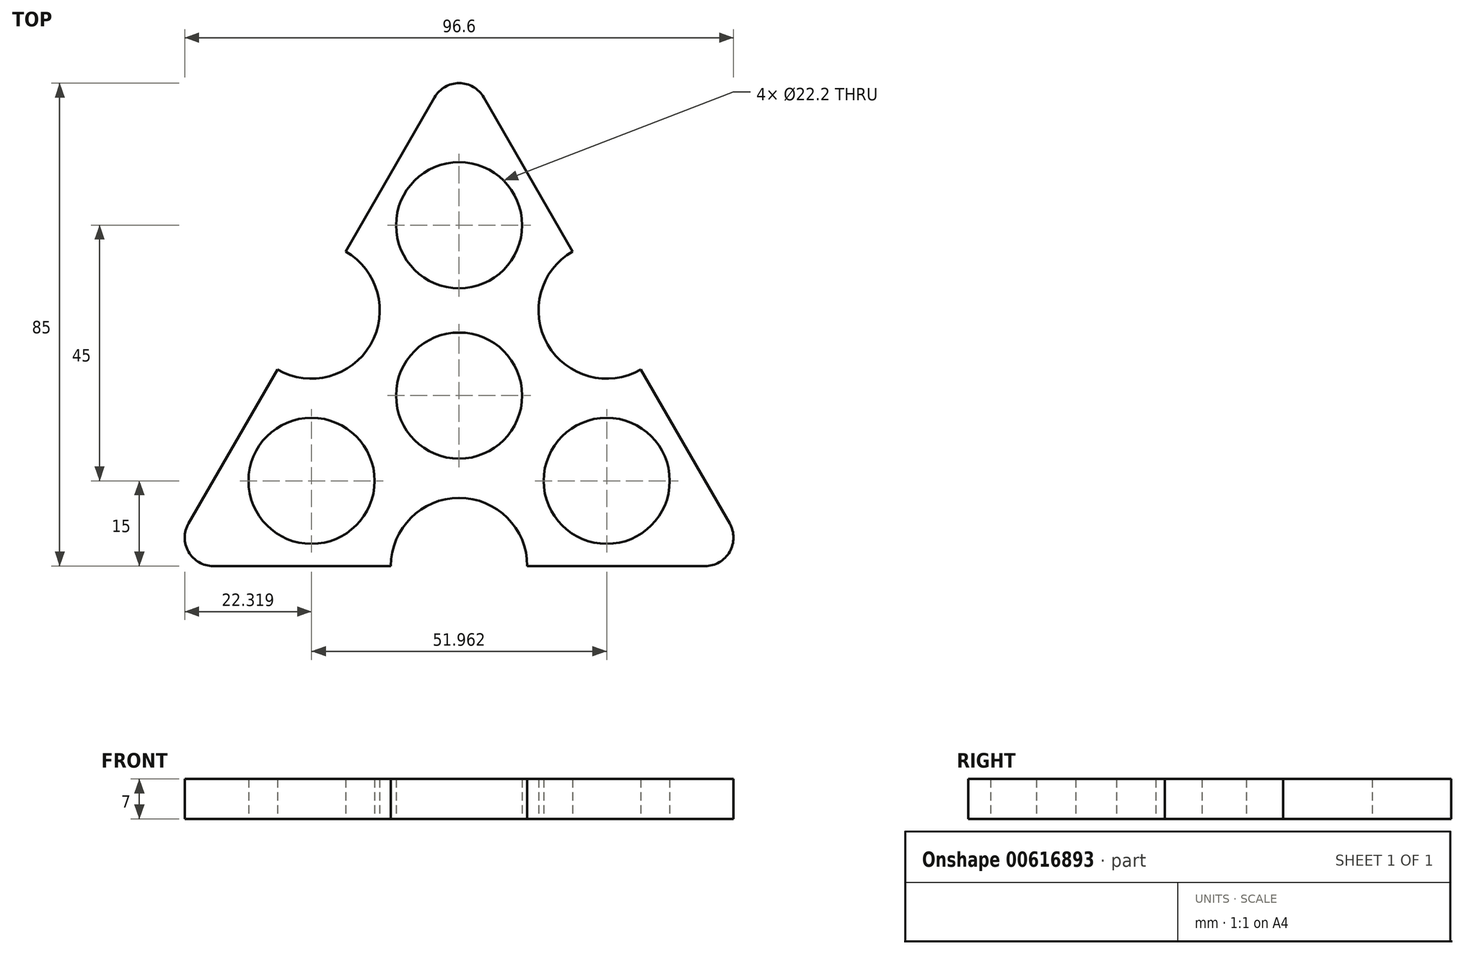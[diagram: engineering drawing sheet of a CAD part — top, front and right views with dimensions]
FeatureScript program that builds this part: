
annotation { "Feature Type Name" : "Feature", "Feature Type Description" : "" }
export const myFeature = defineFeature(function(context is Context, id is Id, definition is map)
    precondition{}
    {
        {
            var Q0;
            Q0=qCreatedBy(makeId("Top.planeOp"),FACE);
            var sketch = newSketch(context, id + "F0", { "sketchPlane" : qUnion([Q0])});
            skCircle(sketch, "E0", {"center": v(0, 0) * mm, "radius": 11.1 * mm});
            skCircle(sketch, "E1", {"center": v(0, 30) * mm, "radius": 11.1 * mm});
            skCircle(sketch, "E2.1.0", {"center": v(-25.98, -15) * mm, "radius": 11.1 * mm});
            skCircle(sketch, "E2.2.0", {"center": v(25.98, -15) * mm, "radius": 11.1 * mm});
            skLineSegment(sketch, "E3", {"start": v(0, 60) * mm, "end": v(-19.98, 25.4) * mm});
            skLineSegment(sketch, "E4", {"start": v(51.96, -30) * mm, "end": v(12, -30) * mm});
            skLineSegment(sketch, "E5", {"start": v(51.96, -30) * mm, "end": v(31.98, 4.6) * mm});
            skArc(sketch, "E6", {"start": v(-31.98, 4.6) * mm, "mid": v(-15.59, 9) * mm, "end": v(-19.98, 25.4) * mm});
            skArc(sketch, "E7", {"start": v(19.98, 25.4) * mm, "mid": v(15.59, 9) * mm, "end": v(31.98, 4.6) * mm});
            skArc(sketch, "E8", {"start": v(12, -30) * mm, "mid": v(0, -18) * mm, "end": v(-12, -30) * mm});
            skLineSegment(sketch, "E9.trimOffspring", {"start": v(-31.98, 4.6) * mm, "end": v(-51.96, -30) * mm});
            skLineSegment(sketch, "E10.trimOffspring", {"start": v(-12, -30) * mm, "end": v(-51.96, -30) * mm});
            skLineSegment(sketch, "E11.trimOffspring", {"start": v(19.98, 25.4) * mm, "end": v(0, 60) * mm});
            skSolve(sketch);
        }
        {
            var Q0;
            Q0=makeQuery(id+"F0.imprint","IMPRINT",FACE,{"disambiguationData":[TD([[makeQuery(id+"F0.imprint","IMPRINT",EDGE,{"derivedFrom":sQuery(id+"F0.wireOp",EDGE,"E0")}),-1.0]])]});
            extrude(context, id + "F1", {"entities" : qUnion([Q0]), "depth" : 7 * mm, "offsetDistance" : 25 * mm});
        }
        {
            var Q0;
            Q0=makeQuery(id+"F1.opExtrude","SWEPT_EDGE",EDGE,{"disambiguationData":[OSD([sQuery(id+"F0.wireOp",EDGE,"E3"),sQuery(id+"F0.wireOp",EDGE,"E11.trimOffspring")])]});
            var Q1;
            Q1=makeQuery(id+"F1.opExtrude","SWEPT_EDGE",EDGE,{"disambiguationData":[OSD([sQuery(id+"F0.wireOp",EDGE,"E4"),sQuery(id+"F0.wireOp",EDGE,"E5")])]});
            var Q2;
            Q2=makeQuery(id+"F1.opExtrude","SWEPT_EDGE",EDGE,{"disambiguationData":[OSD([sQuery(id+"F0.wireOp",EDGE,"E9.trimOffspring"),sQuery(id+"F0.wireOp",EDGE,"E10.trimOffspring")])]});
            fillet(context, id + "F2", {"entities" : qUnion([Q0, Q1, Q2]), "radius" : 5 * mm, "tangentPropagation" : true, "allowEdgeOverflow" : false});
        }
    });
